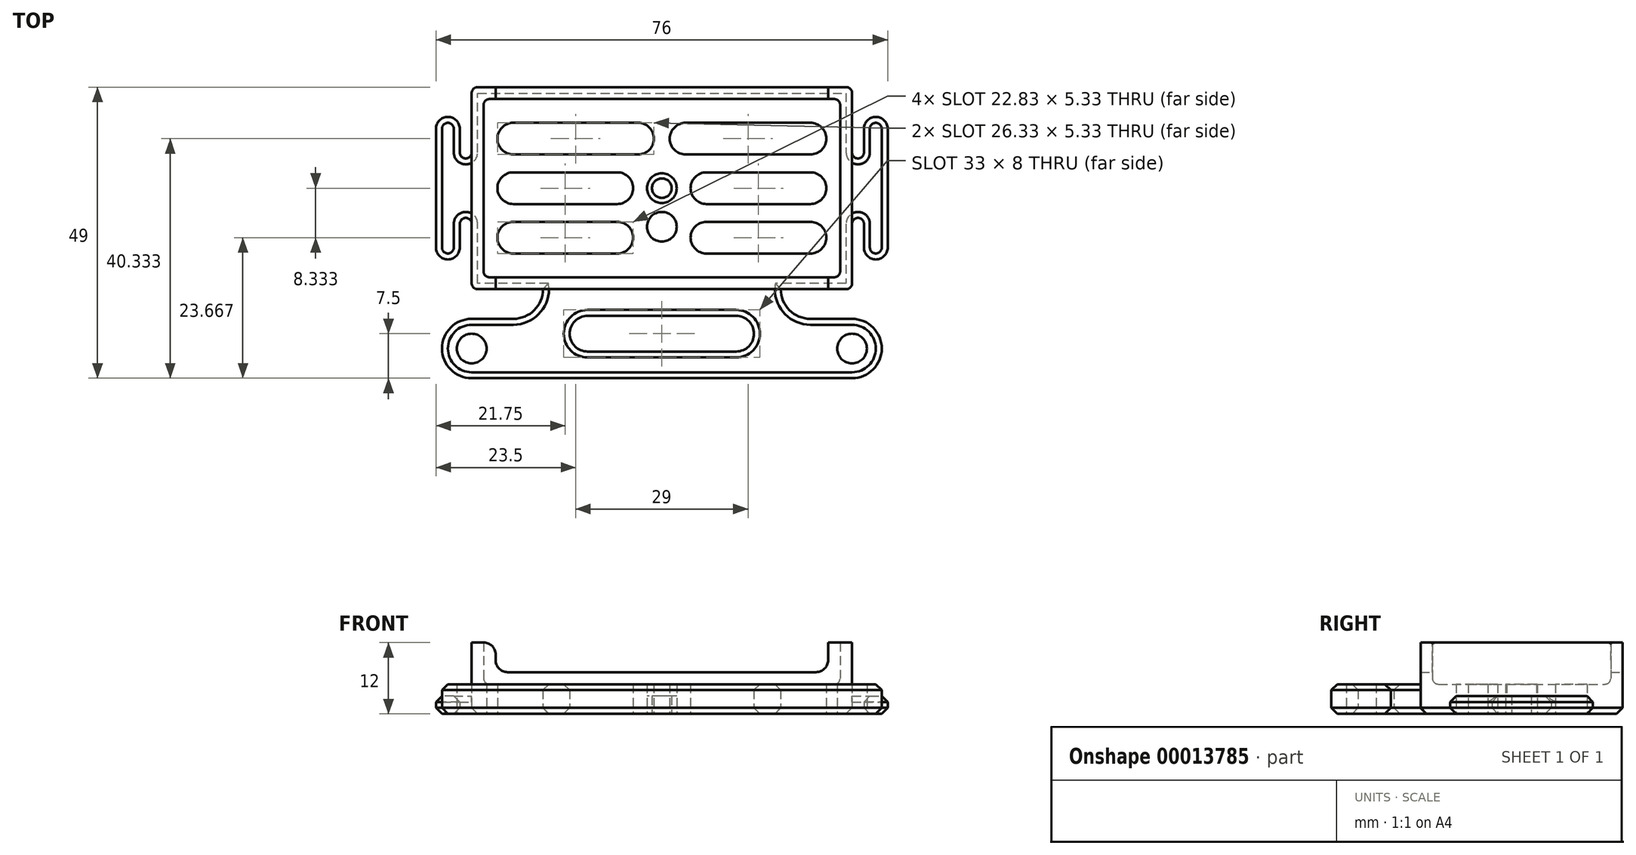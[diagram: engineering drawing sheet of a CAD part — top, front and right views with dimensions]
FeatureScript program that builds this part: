
annotation { "Feature Type Name" : "Feature", "Feature Type Description" : "" }
export const myFeature = defineFeature(function(context is Context, id is Id, definition is map)
    precondition{}
    {
        {
            var Q0;
            Q0=qCreatedBy(makeId("Top.planeOp"),FACE);
            var sketch = newSketch(context, id + "F0", { "sketchPlane" : qUnion([Q0])});
            skCircle(sketch, "E0", {"center": v(0, 0) * mm, "radius": 2.5 * mm});
            skCircle(sketch, "E1", {"center": v(0, -6.5) * mm, "radius": 2.5 * mm});
            skLineSegment(sketch, "E2", {"start": v(0, -6.5) * mm, "end": v(0, 17) * mm, "construction": true});
            skLineSegment(sketch, "E3.rect.bottom", {"start": v(-32, 17) * mm, "end": v(32, 17) * mm});
            skLineSegment(sketch, "E3.rect.top", {"start": v(-32, -17) * mm, "end": v(32, -17) * mm});
            skLineSegment(sketch, "E3.rect.left", {"start": v(-32, 17) * mm, "end": v(-32, -17) * mm});
            skLineSegment(sketch, "E3.rect.right", {"start": v(32, 17) * mm, "end": v(32, -17) * mm});
            skLineSegment(sketch, "E4.bottom", {"start": v(-32, -22) * mm, "end": v(-25, -22) * mm});
            skLineSegment(sketch, "E4.top", {"start": v(-32, -32) * mm, "end": v(32, -32) * mm});
            skLineSegment(sketch, "E4.left", {"start": v(-32, -22) * mm, "end": v(-32, -32) * mm, "construction": true});
            skLineSegment(sketch, "E4.right", {"start": v(32, -22) * mm, "end": v(32, -32) * mm, "construction": true});
            skCircle(sketch, "E5", {"center": v(-32, -27) * mm, "radius": 2.5 * mm});
            skArc(sketch, "E6", {"start": v(-32, -32) * mm, "mid": v(-37, -27) * mm, "end": v(-32, -22) * mm});
            skLineSegment(sketch, "E7", {"start": v(-20, -17) * mm, "end": v(-20, -17) * mm});
            skLineSegment(sketch, "E8.0.MirrorCS", {"start": v(20, -17) * mm, "end": v(20, -22) * mm});
            skCircle(sketch, "E9.0.MirrorC", {"center": v(32, -27) * mm, "radius": 2.5 * mm});
            skArc(sketch, "E10.0.MirrorCS", {"start": v(32, -32) * mm, "mid": v(37, -27) * mm, "end": v(32, -22) * mm});
            skPoint(sketch, "E11.newPointA", {"position": v(-20, -22) * mm});
            skArc(sketch, "E11.filletArc", {"start": v(-25, -22) * mm, "mid": v(-21.46, -20.54) * mm, "end": v(-20, -17) * mm});
            skArc(sketch, "E12.0.MirrorCS", {"start": v(25, -22) * mm, "mid": v(21.46, -20.54) * mm, "end": v(20, -17) * mm});
            skLineSegment(sketch, "E13", {"start": v(32, -22) * mm, "end": v(25, -22) * mm});
            skLineSegment(sketch, "E14.rect.bottom", {"start": v(12.5, -27.5) * mm, "end": v(-12.5, -27.5) * mm});
            skLineSegment(sketch, "E14.rect.top", {"start": v(12.5, -21.5) * mm, "end": v(-12.5, -21.5) * mm});
            skLineSegment(sketch, "E14.rect.left", {"start": v(12.5, -27.5) * mm, "end": v(12.5, -21.5) * mm, "construction": true});
            skLineSegment(sketch, "E14.rect.right", {"start": v(-12.5, -27.5) * mm, "end": v(-12.5, -21.5) * mm, "construction": true});
            skPoint(sketch, "E14.rect.middle", {"position": v(0, -24.5) * mm});
            skLineSegment(sketch, "E15", {"start": v(0, -17) * mm, "end": v(0, -32) * mm, "construction": true});
            skArc(sketch, "E16", {"start": v(-12.5, -21.5) * mm, "mid": v(-15.5, -24.5) * mm, "end": v(-12.5, -27.5) * mm});
            skArc(sketch, "E17", {"start": v(12.5, -21.5) * mm, "mid": v(15.5, -24.5) * mm, "end": v(12.5, -27.5) * mm});
            skLineSegment(sketch, "E18.0", {"start": v(-30, 15) * mm, "end": v(30, 15) * mm});
            skLineSegment(sketch, "E18.1", {"start": v(-30, 15) * mm, "end": v(-30, -15) * mm});
            skLineSegment(sketch, "E18.2", {"start": v(-30, -15) * mm, "end": v(30, -15) * mm});
            skLineSegment(sketch, "E18.3", {"start": v(30, 15) * mm, "end": v(30, -15) * mm});
            skLineSegment(sketch, "E19.rect.bottom", {"start": v(-38, 10) * mm, "end": v(-34, 10) * mm, "construction": true});
            skLineSegment(sketch, "E19.rect.top", {"start": v(-38, -10) * mm, "end": v(-34, -10) * mm, "construction": true});
            skLineSegment(sketch, "E19.rect.left", {"start": v(-38, 10) * mm, "end": v(-38, -10) * mm});
            skLineSegment(sketch, "E19.rect.right", {"start": v(-34, 10) * mm, "end": v(-34, 6) * mm});
            skPoint(sketch, "E19.rect.middle", {"position": v(-36, 0) * mm});
            skArc(sketch, "E20", {"start": v(-38, -10) * mm, "mid": v(-36, -12) * mm, "end": v(-34, -10) * mm});
            skArc(sketch, "E21", {"start": v(-38, 10) * mm, "mid": v(-36, 12) * mm, "end": v(-34, 10) * mm});
            skLineSegment(sketch, "E22", {"start": v(0, 0) * mm, "end": v(-36, 0) * mm, "construction": true});
            skArc(sketch, "E23.filletArc", {"start": v(-34, 6) * mm, "mid": v(-33, 5) * mm, "end": v(-32, 6) * mm});
            skArc(sketch, "E24.0.MirrorCS", {"start": v(-34, -6) * mm, "mid": v(-33, -5) * mm, "end": v(-32, -6) * mm});
            skLineSegment(sketch, "E25.0.MirrorCS", {"start": v(-34, -10) * mm, "end": v(-34, -6) * mm});
            skArc(sketch, "E26.0.MirrorCS", {"start": v(34, -6) * mm, "mid": v(33, -5) * mm, "end": v(32, -6) * mm});
            skLineSegment(sketch, "E26.1.MirrorCS", {"start": v(38, 10) * mm, "end": v(34, 10) * mm, "construction": true});
            skLineSegment(sketch, "E26.2.MirrorCS", {"start": v(38, -10) * mm, "end": v(34, -10) * mm, "construction": true});
            skArc(sketch, "E26.3.MirrorCS", {"start": v(38, 10) * mm, "mid": v(36, 12) * mm, "end": v(34, 10) * mm});
            skLineSegment(sketch, "E26.4.MirrorCS", {"start": v(34, -10) * mm, "end": v(34, -6) * mm});
            skLineSegment(sketch, "E26.5.MirrorCS", {"start": v(38, 10) * mm, "end": v(38, -10) * mm});
            skLineSegment(sketch, "E26.6.MirrorCS", {"start": v(34, 10) * mm, "end": v(34, 6) * mm});
            skArc(sketch, "E26.7.MirrorCS", {"start": v(38, -10) * mm, "mid": v(36, -12) * mm, "end": v(34, -10) * mm});
            skPoint(sketch, "E26.8.MirrorP", {"position": v(36, 0) * mm});
            skArc(sketch, "E26.9.MirrorCS", {"start": v(34, 6) * mm, "mid": v(33, 5) * mm, "end": v(32, 6) * mm});
            skLineSegment(sketch, "E27.bottom", {"start": v(-25, 11) * mm, "end": v(-4, 11) * mm});
            skLineSegment(sketch, "E27.top", {"start": v(-25, 5.67) * mm, "end": v(-4, 5.67) * mm});
            skLineSegment(sketch, "E27.left", {"start": v(-25, 11) * mm, "end": v(-25, 5.67) * mm, "construction": true});
            skLineSegment(sketch, "E27.right", {"start": v(-4, 11) * mm, "end": v(-4, 5.67) * mm, "construction": true});
            skLineSegment(sketch, "E28.bottom", {"start": v(-25, 2.67) * mm, "end": v(-7.5, 2.67) * mm});
            skLineSegment(sketch, "E28.top", {"start": v(-25, -2.67) * mm, "end": v(-7.5, -2.67) * mm});
            skLineSegment(sketch, "E28.left", {"start": v(-25, 2.67) * mm, "end": v(-25, -2.67) * mm, "construction": true});
            skLineSegment(sketch, "E28.right", {"start": v(-7.5, 2.67) * mm, "end": v(-7.5, -2.67) * mm, "construction": true});
            skLineSegment(sketch, "E29.bottom", {"start": v(-25, -5.67) * mm, "end": v(-7.5, -5.67) * mm});
            skLineSegment(sketch, "E29.top", {"start": v(-25, -11) * mm, "end": v(-7.5, -11) * mm});
            skLineSegment(sketch, "E29.left", {"start": v(-25, -5.67) * mm, "end": v(-25, -11) * mm, "construction": true});
            skLineSegment(sketch, "E29.right", {"start": v(-7.5, -5.67) * mm, "end": v(-7.5, -11) * mm, "construction": true});
            skPoint(sketch, "E30", {"position": v(-25, 0) * mm});
            skLineSegment(sketch, "E31.0.MirrorCS", {"start": v(25, -11) * mm, "end": v(7.5, -11) * mm});
            skLineSegment(sketch, "E32.0.MirrorCS", {"start": v(25, -5.67) * mm, "end": v(7.5, -5.67) * mm});
            skLineSegment(sketch, "E33.0.MirrorCS", {"start": v(25, -2.67) * mm, "end": v(7.5, -2.67) * mm});
            skLineSegment(sketch, "E34.0.MirrorCS", {"start": v(25, 2.67) * mm, "end": v(7.5, 2.67) * mm});
            skLineSegment(sketch, "E35.0.MirrorCS", {"start": v(25, 5.67) * mm, "end": v(4, 5.67) * mm});
            skLineSegment(sketch, "E36.0.MirrorCS", {"start": v(25, 11) * mm, "end": v(4, 11) * mm});
            skLineSegment(sketch, "E37.0.MirrorCS", {"start": v(4, 11) * mm, "end": v(4, 5.67) * mm, "construction": true});
            skLineSegment(sketch, "E38.0.MirrorCS", {"start": v(7.5, 2.67) * mm, "end": v(7.5, -2.67) * mm, "construction": true});
            skLineSegment(sketch, "E39.0.MirrorCS", {"start": v(7.5, -5.67) * mm, "end": v(7.5, -11) * mm, "construction": true});
            skLineSegment(sketch, "E40.0.MirrorCS", {"start": v(25, -5.67) * mm, "end": v(25, -11) * mm, "construction": true});
            skLineSegment(sketch, "E41.0.MirrorCS", {"start": v(25, 2.67) * mm, "end": v(25, -2.67) * mm, "construction": true});
            skLineSegment(sketch, "E42.0.MirrorCS", {"start": v(25, 11) * mm, "end": v(25, 5.67) * mm, "construction": true});
            skArc(sketch, "E43", {"start": v(-25, 11) * mm, "mid": v(-27.67, 8.33) * mm, "end": v(-25, 5.67) * mm});
            skArc(sketch, "E44", {"start": v(-25, 2.67) * mm, "mid": v(-27.67, 0) * mm, "end": v(-25, -2.67) * mm});
            skArc(sketch, "E45", {"start": v(-25, -5.67) * mm, "mid": v(-27.67, -8.33) * mm, "end": v(-25, -11) * mm});
            skArc(sketch, "E46", {"start": v(-4, 11) * mm, "mid": v(-1.33, 8.33) * mm, "end": v(-4, 5.67) * mm});
            skArc(sketch, "E47", {"start": v(-7.5, 2.67) * mm, "mid": v(-4.83, 0) * mm, "end": v(-7.5, -2.67) * mm});
            skArc(sketch, "E48", {"start": v(-7.5, -5.67) * mm, "mid": v(-4.83, -8.33) * mm, "end": v(-7.5, -11) * mm});
            skArc(sketch, "E49.0.MirrorCS", {"start": v(4, 11) * mm, "mid": v(1.33, 8.33) * mm, "end": v(4, 5.67) * mm});
            skArc(sketch, "E50.0.MirrorCS", {"start": v(7.5, 2.67) * mm, "mid": v(4.83, 0) * mm, "end": v(7.5, -2.67) * mm});
            skArc(sketch, "E51.0.MirrorCS", {"start": v(7.5, -5.67) * mm, "mid": v(4.83, -8.33) * mm, "end": v(7.5, -11) * mm});
            skArc(sketch, "E52.0.MirrorCS", {"start": v(25, 11) * mm, "mid": v(27.67, 8.33) * mm, "end": v(25, 5.67) * mm});
            skArc(sketch, "E53.0.MirrorCS", {"start": v(25, 2.67) * mm, "mid": v(27.67, 0) * mm, "end": v(25, -2.67) * mm});
            skArc(sketch, "E54.0.MirrorCS", {"start": v(25, -5.67) * mm, "mid": v(27.67, -8.33) * mm, "end": v(25, -11) * mm});
            skCircle(sketch, "E55", {"center": v(0, 0) * mm, "radius": 1.65 * mm});
            skSolve(sketch);
        }
        {
            var Q0;
            Q0=makeQuery(id+"F0.imprint","IMPRINT",FACE,{"disambiguationData":[TD([[makeQuery(id+"F0.imprint","IMPRINT",EDGE,{"derivedFrom":sQuery(id+"F0.wireOp",EDGE,"E4.bottom")}),-1.0]])]});
            var Q1;
            Q1=makeQuery(id+"F0.imprint","IMPRINT",FACE,{"disambiguationData":[TD([[makeQuery(id+"F0.imprint","IMPRINT",EDGE,{"derivedFrom":sQuery(id+"F0.wireOp",EDGE,"E0")}),-1.0]])]});
            var Q2;
            {var subQ5=sQuery(id+"F0.wireOp",EDGE,"E3.rect.bottom");Q2=makeQuery(id+"F0.imprint","IMPRINT",FACE,{"disambiguationData":[TD([[makeQuery(id+"F0.imprint","IMPRINT",EDGE,{"derivedFrom":subQ5}),-1.0]])]});}
            extrude(context, id + "F1", {"entities" : qUnion([Q0, Q1, Q2]), "depth" : 5 * mm});
        }
        {
            var Q0;
            Q0=makeQuery(id+"F0.imprint","IMPRINT",FACE,{"disambiguationData":[TD([[makeQuery(id+"F0.imprint","IMPRINT",EDGE,{"derivedFrom":sQuery(id+"F0.wireOp",EDGE,"E19.rect.left")}),1.0]])]});
            var Q1;
            {var subQ1=sQuery(id+"F0.wireOp",EDGE,"E26.0.MirrorCS");Q1=makeQuery(id+"F0.imprint","IMPRINT",FACE,{"disambiguationData":[TD([[makeQuery(id+"F0.imprint","IMPRINT",EDGE,{"derivedFrom":subQ1}),-1.0]])]});}
            var Q2;
            Q2=makeQuery(id+"F0.imprint","IMPRINT",FACE,{"disambiguationData":[TD([[makeQuery(id+"F0.imprint","IMPRINT",EDGE,{"derivedFrom":sQuery(id+"F0.wireOp",EDGE,"E0")}),1.0]])]});
            extrude(context, id + "F2", {"entities" : qUnion([Q0, Q1, Q2]), "operationType" : NewBodyOperationType.ADD, "depth" : 3 * mm});
        }
        {
            var Q0;
            {var subQ5=sQuery(id+"F0.wireOp",EDGE,"E3.rect.bottom");Q0=makeQuery(id+"F0.imprint","IMPRINT",FACE,{"disambiguationData":[TD([[makeQuery(id+"F0.imprint","IMPRINT",EDGE,{"derivedFrom":subQ5}),-1.0]])]});}
            extrude(context, id + "F3", {"entities" : qUnion([Q0]), "operationType" : NewBodyOperationType.ADD, "depth" : 12 * mm});
        }
        {
            var Q0;
            Q0=makeQuery(id+"F3.opExtrude","SWEPT_FACE",FACE,{"disambiguationData":[OSD([sQuery(id+"F0.wireOp",EDGE,"E18.2")])]});
            var sketch = newSketch(context, id + "F4", { "sketchPlane" : qUnion([Q0])});
            skLineSegment(sketch, "E56.bottom", {"start": v(-30, 5) * mm, "end": v(30, 5) * mm, "construction": true});
            skLineSegment(sketch, "E56.top", {"start": v(-30, 12) * mm, "end": v(30, 12) * mm});
            skLineSegment(sketch, "E56.left", {"start": v(-30, 5) * mm, "end": v(-30, 12) * mm, "construction": true});
            skLineSegment(sketch, "E56.right", {"start": v(30, 5) * mm, "end": v(30, 12) * mm, "construction": true});
            skLineSegment(sketch, "E57.0", {"start": v(-27.97, 7.03) * mm, "end": v(27.97, 7.03) * mm});
            skLineSegment(sketch, "E57.1", {"start": v(-27.97, 7.03) * mm, "end": v(-27.97, 12) * mm});
            skLineSegment(sketch, "E58", {"start": v(0, 0) * mm, "end": v(0, 12) * mm, "construction": true});
            skLineSegment(sketch, "E59.0.MirrorCS", {"start": v(27.97, 7.03) * mm, "end": v(27.97, 12) * mm});
            skSolve(sketch);
        }
        {
            var Q0;
            Q0=makeQuery(id+"F4.imprint","IMPRINT",FACE,{"disambiguationData":[TD([[makeQuery(id+"F4.imprint","IMPRINT",EDGE,{"derivedFrom":sQuery(id+"F4.wireOp",EDGE,"E57.0")}),1.0]])]});
            var Q1;
            Q1=sQuery(id+"F4.wireOp",EDGE,"E56.top");
            extrude(context, id + "F5", {"entities" : qUnion([Q0]), "operationType" : NewBodyOperationType.REMOVE, "surfaceEntities" : qUnion([Q1]), "endBound" : BoundingType.SYMMETRIC, "oppositeDirection" : true, "depth" : 99.9 * mm});
        }
        {
            var Q0;
            Q0=makeQuery(id+"F3.boolean.opBoolean","INTERSECT",EDGE,{"derivedFrom":[makeQuery(id+"F1.opExtrude","CAP_FACE",FACE,{"disambiguationData":[OSD([sQuery(id+"F0.wireOp",EDGE,"E0"),sQuery(id+"F0.wireOp",EDGE,"E1"),sQuery(id+"F0.wireOp",EDGE,"E3.rect.bottom"),sQuery(id+"F0.wireOp",EDGE,"E3.rect.top"),sQuery(id+"F0.wireOp",EDGE,"E3.rect.left"),sQuery(id+"F0.wireOp",EDGE,"E3.rect.right"),sQuery(id+"F0.wireOp",EDGE,"E4.bottom"),sQuery(id+"F0.wireOp",EDGE,"E4.top"),sQuery(id+"F0.wireOp",EDGE,"E5"),sQuery(id+"F0.wireOp",EDGE,"E6"),sQuery(id+"F0.wireOp",EDGE,"E9.0.MirrorC"),sQuery(id+"F0.wireOp",EDGE,"E10.0.MirrorCS"),sQuery(id+"F0.wireOp",EDGE,"E11.filletArc"),sQuery(id+"F0.wireOp",EDGE,"E12.0.MirrorCS"),sQuery(id+"F0.wireOp",EDGE,"E13"),sQuery(id+"F0.wireOp",EDGE,"E14.rect.bottom"),sQuery(id+"F0.wireOp",EDGE,"E14.rect.top"),sQuery(id+"F0.wireOp",EDGE,"E16"),sQuery(id+"F0.wireOp",EDGE,"E17"),sQuery(id+"F0.wireOp",EDGE,"E27.bottom"),sQuery(id+"F0.wireOp",EDGE,"E27.top"),sQuery(id+"F0.wireOp",EDGE,"E28.bottom"),sQuery(id+"F0.wireOp",EDGE,"E28.top"),sQuery(id+"F0.wireOp",EDGE,"E29.bottom"),sQuery(id+"F0.wireOp",EDGE,"E29.top"),sQuery(id+"F0.wireOp",EDGE,"E31.0.MirrorCS"),sQuery(id+"F0.wireOp",EDGE,"E32.0.MirrorCS"),sQuery(id+"F0.wireOp",EDGE,"E33.0.MirrorCS"),sQuery(id+"F0.wireOp",EDGE,"E34.0.MirrorCS"),sQuery(id+"F0.wireOp",EDGE,"E35.0.MirrorCS"),sQuery(id+"F0.wireOp",EDGE,"E36.0.MirrorCS"),sQuery(id+"F0.wireOp",EDGE,"E43"),sQuery(id+"F0.wireOp",EDGE,"E44"),sQuery(id+"F0.wireOp",EDGE,"E45"),sQuery(id+"F0.wireOp",EDGE,"E46"),sQuery(id+"F0.wireOp",EDGE,"E47"),sQuery(id+"F0.wireOp",EDGE,"E48"),sQuery(id+"F0.wireOp",EDGE,"E49.0.MirrorCS"),sQuery(id+"F0.wireOp",EDGE,"E50.0.MirrorCS"),sQuery(id+"F0.wireOp",EDGE,"E51.0.MirrorCS"),sQuery(id+"F0.wireOp",EDGE,"E52.0.MirrorCS"),sQuery(id+"F0.wireOp",EDGE,"E53.0.MirrorCS"),sQuery(id+"F0.wireOp",EDGE,"E54.0.MirrorCS")])],"isStart":false}),makeQuery(id+"F3.opExtrude","SWEPT_FACE",FACE,{"disambiguationData":[OSD([sQuery(id+"F0.wireOp",EDGE,"E18.1")])]})]});
            var Q1;
            Q1=makeQuery(id+"F3.boolean.opBoolean","INTERSECT",EDGE,{"derivedFrom":[makeQuery(id+"F1.opExtrude","CAP_FACE",FACE,{"disambiguationData":[OSD([sQuery(id+"F0.wireOp",EDGE,"E0"),sQuery(id+"F0.wireOp",EDGE,"E1"),sQuery(id+"F0.wireOp",EDGE,"E3.rect.bottom"),sQuery(id+"F0.wireOp",EDGE,"E3.rect.top"),sQuery(id+"F0.wireOp",EDGE,"E3.rect.left"),sQuery(id+"F0.wireOp",EDGE,"E3.rect.right"),sQuery(id+"F0.wireOp",EDGE,"E4.bottom"),sQuery(id+"F0.wireOp",EDGE,"E4.top"),sQuery(id+"F0.wireOp",EDGE,"E5"),sQuery(id+"F0.wireOp",EDGE,"E6"),sQuery(id+"F0.wireOp",EDGE,"E9.0.MirrorC"),sQuery(id+"F0.wireOp",EDGE,"E10.0.MirrorCS"),sQuery(id+"F0.wireOp",EDGE,"E11.filletArc"),sQuery(id+"F0.wireOp",EDGE,"E12.0.MirrorCS"),sQuery(id+"F0.wireOp",EDGE,"E13"),sQuery(id+"F0.wireOp",EDGE,"E14.rect.bottom"),sQuery(id+"F0.wireOp",EDGE,"E14.rect.top"),sQuery(id+"F0.wireOp",EDGE,"E16"),sQuery(id+"F0.wireOp",EDGE,"E17"),sQuery(id+"F0.wireOp",EDGE,"E27.bottom"),sQuery(id+"F0.wireOp",EDGE,"E27.top"),sQuery(id+"F0.wireOp",EDGE,"E28.bottom"),sQuery(id+"F0.wireOp",EDGE,"E28.top"),sQuery(id+"F0.wireOp",EDGE,"E29.bottom"),sQuery(id+"F0.wireOp",EDGE,"E29.top"),sQuery(id+"F0.wireOp",EDGE,"E31.0.MirrorCS"),sQuery(id+"F0.wireOp",EDGE,"E32.0.MirrorCS"),sQuery(id+"F0.wireOp",EDGE,"E33.0.MirrorCS"),sQuery(id+"F0.wireOp",EDGE,"E34.0.MirrorCS"),sQuery(id+"F0.wireOp",EDGE,"E35.0.MirrorCS"),sQuery(id+"F0.wireOp",EDGE,"E36.0.MirrorCS"),sQuery(id+"F0.wireOp",EDGE,"E43"),sQuery(id+"F0.wireOp",EDGE,"E44"),sQuery(id+"F0.wireOp",EDGE,"E45"),sQuery(id+"F0.wireOp",EDGE,"E46"),sQuery(id+"F0.wireOp",EDGE,"E47"),sQuery(id+"F0.wireOp",EDGE,"E48"),sQuery(id+"F0.wireOp",EDGE,"E49.0.MirrorCS"),sQuery(id+"F0.wireOp",EDGE,"E50.0.MirrorCS"),sQuery(id+"F0.wireOp",EDGE,"E51.0.MirrorCS"),sQuery(id+"F0.wireOp",EDGE,"E52.0.MirrorCS"),sQuery(id+"F0.wireOp",EDGE,"E53.0.MirrorCS"),sQuery(id+"F0.wireOp",EDGE,"E54.0.MirrorCS")])],"isStart":false}),makeQuery(id+"F3.opExtrude","SWEPT_FACE",FACE,{"disambiguationData":[OSD([sQuery(id+"F0.wireOp",EDGE,"E18.0")])]})]});
            var Q2;
            Q2=makeQuery(id+"F3.boolean.opBoolean","INTERSECT",EDGE,{"derivedFrom":[makeQuery(id+"F1.opExtrude","CAP_FACE",FACE,{"disambiguationData":[OSD([sQuery(id+"F0.wireOp",EDGE,"E0"),sQuery(id+"F0.wireOp",EDGE,"E1"),sQuery(id+"F0.wireOp",EDGE,"E3.rect.bottom"),sQuery(id+"F0.wireOp",EDGE,"E3.rect.top"),sQuery(id+"F0.wireOp",EDGE,"E3.rect.left"),sQuery(id+"F0.wireOp",EDGE,"E3.rect.right"),sQuery(id+"F0.wireOp",EDGE,"E4.bottom"),sQuery(id+"F0.wireOp",EDGE,"E4.top"),sQuery(id+"F0.wireOp",EDGE,"E5"),sQuery(id+"F0.wireOp",EDGE,"E6"),sQuery(id+"F0.wireOp",EDGE,"E9.0.MirrorC"),sQuery(id+"F0.wireOp",EDGE,"E10.0.MirrorCS"),sQuery(id+"F0.wireOp",EDGE,"E11.filletArc"),sQuery(id+"F0.wireOp",EDGE,"E12.0.MirrorCS"),sQuery(id+"F0.wireOp",EDGE,"E13"),sQuery(id+"F0.wireOp",EDGE,"E14.rect.bottom"),sQuery(id+"F0.wireOp",EDGE,"E14.rect.top"),sQuery(id+"F0.wireOp",EDGE,"E16"),sQuery(id+"F0.wireOp",EDGE,"E17"),sQuery(id+"F0.wireOp",EDGE,"E27.bottom"),sQuery(id+"F0.wireOp",EDGE,"E27.top"),sQuery(id+"F0.wireOp",EDGE,"E28.bottom"),sQuery(id+"F0.wireOp",EDGE,"E28.top"),sQuery(id+"F0.wireOp",EDGE,"E29.bottom"),sQuery(id+"F0.wireOp",EDGE,"E29.top"),sQuery(id+"F0.wireOp",EDGE,"E31.0.MirrorCS"),sQuery(id+"F0.wireOp",EDGE,"E32.0.MirrorCS"),sQuery(id+"F0.wireOp",EDGE,"E33.0.MirrorCS"),sQuery(id+"F0.wireOp",EDGE,"E34.0.MirrorCS"),sQuery(id+"F0.wireOp",EDGE,"E35.0.MirrorCS"),sQuery(id+"F0.wireOp",EDGE,"E36.0.MirrorCS"),sQuery(id+"F0.wireOp",EDGE,"E43"),sQuery(id+"F0.wireOp",EDGE,"E44"),sQuery(id+"F0.wireOp",EDGE,"E45"),sQuery(id+"F0.wireOp",EDGE,"E46"),sQuery(id+"F0.wireOp",EDGE,"E47"),sQuery(id+"F0.wireOp",EDGE,"E48"),sQuery(id+"F0.wireOp",EDGE,"E49.0.MirrorCS"),sQuery(id+"F0.wireOp",EDGE,"E50.0.MirrorCS"),sQuery(id+"F0.wireOp",EDGE,"E51.0.MirrorCS"),sQuery(id+"F0.wireOp",EDGE,"E52.0.MirrorCS"),sQuery(id+"F0.wireOp",EDGE,"E53.0.MirrorCS"),sQuery(id+"F0.wireOp",EDGE,"E54.0.MirrorCS")])],"isStart":false}),makeQuery(id+"F3.opExtrude","SWEPT_FACE",FACE,{"disambiguationData":[OSD([sQuery(id+"F0.wireOp",EDGE,"E18.2")])]})]});
            var Q3;
            Q3=makeQuery(id+"F3.boolean.opBoolean","INTERSECT",EDGE,{"derivedFrom":[makeQuery(id+"F1.opExtrude","CAP_FACE",FACE,{"disambiguationData":[OSD([sQuery(id+"F0.wireOp",EDGE,"E0"),sQuery(id+"F0.wireOp",EDGE,"E1"),sQuery(id+"F0.wireOp",EDGE,"E3.rect.bottom"),sQuery(id+"F0.wireOp",EDGE,"E3.rect.top"),sQuery(id+"F0.wireOp",EDGE,"E3.rect.left"),sQuery(id+"F0.wireOp",EDGE,"E3.rect.right"),sQuery(id+"F0.wireOp",EDGE,"E4.bottom"),sQuery(id+"F0.wireOp",EDGE,"E4.top"),sQuery(id+"F0.wireOp",EDGE,"E5"),sQuery(id+"F0.wireOp",EDGE,"E6"),sQuery(id+"F0.wireOp",EDGE,"E9.0.MirrorC"),sQuery(id+"F0.wireOp",EDGE,"E10.0.MirrorCS"),sQuery(id+"F0.wireOp",EDGE,"E11.filletArc"),sQuery(id+"F0.wireOp",EDGE,"E12.0.MirrorCS"),sQuery(id+"F0.wireOp",EDGE,"E13"),sQuery(id+"F0.wireOp",EDGE,"E14.rect.bottom"),sQuery(id+"F0.wireOp",EDGE,"E14.rect.top"),sQuery(id+"F0.wireOp",EDGE,"E16"),sQuery(id+"F0.wireOp",EDGE,"E17"),sQuery(id+"F0.wireOp",EDGE,"E27.bottom"),sQuery(id+"F0.wireOp",EDGE,"E27.top"),sQuery(id+"F0.wireOp",EDGE,"E28.bottom"),sQuery(id+"F0.wireOp",EDGE,"E28.top"),sQuery(id+"F0.wireOp",EDGE,"E29.bottom"),sQuery(id+"F0.wireOp",EDGE,"E29.top"),sQuery(id+"F0.wireOp",EDGE,"E31.0.MirrorCS"),sQuery(id+"F0.wireOp",EDGE,"E32.0.MirrorCS"),sQuery(id+"F0.wireOp",EDGE,"E33.0.MirrorCS"),sQuery(id+"F0.wireOp",EDGE,"E34.0.MirrorCS"),sQuery(id+"F0.wireOp",EDGE,"E35.0.MirrorCS"),sQuery(id+"F0.wireOp",EDGE,"E36.0.MirrorCS"),sQuery(id+"F0.wireOp",EDGE,"E43"),sQuery(id+"F0.wireOp",EDGE,"E44"),sQuery(id+"F0.wireOp",EDGE,"E45"),sQuery(id+"F0.wireOp",EDGE,"E46"),sQuery(id+"F0.wireOp",EDGE,"E47"),sQuery(id+"F0.wireOp",EDGE,"E48"),sQuery(id+"F0.wireOp",EDGE,"E49.0.MirrorCS"),sQuery(id+"F0.wireOp",EDGE,"E50.0.MirrorCS"),sQuery(id+"F0.wireOp",EDGE,"E51.0.MirrorCS"),sQuery(id+"F0.wireOp",EDGE,"E52.0.MirrorCS"),sQuery(id+"F0.wireOp",EDGE,"E53.0.MirrorCS"),sQuery(id+"F0.wireOp",EDGE,"E54.0.MirrorCS")])],"isStart":false}),makeQuery(id+"F3.opExtrude","SWEPT_FACE",FACE,{"disambiguationData":[OSD([sQuery(id+"F0.wireOp",EDGE,"E18.3")])]})]});
            var Q4;
            Q4=makeQuery(id+"F3.opExtrude","SWEPT_EDGE",EDGE,{"disambiguationData":[OSD([sQuery(id+"F0.wireOp",EDGE,"E18.0"),sQuery(id+"F0.wireOp",EDGE,"E18.3")])]});
            var Q5;
            Q5=makeQuery(id+"F3.opExtrude","SWEPT_EDGE",EDGE,{"disambiguationData":[OSD([sQuery(id+"F0.wireOp",EDGE,"E18.0"),sQuery(id+"F0.wireOp",EDGE,"E18.1")])]});
            var Q6;
            Q6=makeQuery(id+"F3.opExtrude","SWEPT_EDGE",EDGE,{"disambiguationData":[OSD([sQuery(id+"F0.wireOp",EDGE,"E18.1"),sQuery(id+"F0.wireOp",EDGE,"E18.2")])]});
            var Q7;
            Q7=makeQuery(id+"F3.opExtrude","SWEPT_EDGE",EDGE,{"disambiguationData":[OSD([sQuery(id+"F0.wireOp",EDGE,"E18.2"),sQuery(id+"F0.wireOp",EDGE,"E18.3")])]});
            var Q8;
            {var subQ0=sQuery(id+"F0.wireOp",EDGE,"E3.rect.bottom");var subQ1=sQuery(id+"F0.wireOp",EDGE,"E3.rect.right");Q8=makeQuery(id+"F3.boolean.opBoolean","MERGE",EDGE,{"derivedFrom":[makeQuery(id+"F1.opExtrude","SWEPT_EDGE",EDGE,{"disambiguationData":[OSD([subQ0,subQ1])]}),makeQuery(id+"F3.opExtrude","SWEPT_EDGE",EDGE,{"disambiguationData":[OSD([subQ0,subQ1])]})]});}
            var Q9;
            {var subQ0=sQuery(id+"F0.wireOp",EDGE,"E3.rect.bottom");var subQ1=sQuery(id+"F0.wireOp",EDGE,"E3.rect.left");Q9=makeQuery(id+"F3.boolean.opBoolean","MERGE",EDGE,{"derivedFrom":[makeQuery(id+"F1.opExtrude","SWEPT_EDGE",EDGE,{"disambiguationData":[OSD([subQ0,subQ1])]}),makeQuery(id+"F3.opExtrude","SWEPT_EDGE",EDGE,{"disambiguationData":[OSD([subQ0,subQ1])]})]});}
            var Q10;
            {var subQ0=sQuery(id+"F0.wireOp",EDGE,"E3.rect.top");var subQ1=sQuery(id+"F0.wireOp",EDGE,"E3.rect.left");Q10=makeQuery(id+"F3.boolean.opBoolean","MERGE",EDGE,{"derivedFrom":[makeQuery(id+"F1.opExtrude","SWEPT_EDGE",EDGE,{"disambiguationData":[OSD([subQ0,subQ1])]}),makeQuery(id+"F3.opExtrude","SWEPT_EDGE",EDGE,{"disambiguationData":[OSD([subQ0,subQ1])]})]});}
            var Q11;
            {var subQ0=sQuery(id+"F0.wireOp",EDGE,"E3.rect.top");var subQ1=sQuery(id+"F0.wireOp",EDGE,"E3.rect.right");Q11=makeQuery(id+"F3.boolean.opBoolean","MERGE",EDGE,{"derivedFrom":[makeQuery(id+"F1.opExtrude","SWEPT_EDGE",EDGE,{"disambiguationData":[OSD([subQ0,subQ1])]}),makeQuery(id+"F3.opExtrude","SWEPT_EDGE",EDGE,{"disambiguationData":[OSD([subQ0,subQ1])]})]});}
            fillet(context, id + "F6", {"entities" : qUnion([Q0, Q1, Q2, Q3, Q4, Q5, Q6, Q7, Q8, Q9, Q10, Q11]), "radius" : 1 * mm, "tangentPropagation" : true, "allowEdgeOverflow" : false});
        }
        {
            var Q0;
            Q0=makeQuery(id+"F5.boolean.opBoolean","COPY",EDGE,{"disambiguationData":[OD(0.0)],"derivedFrom":makeQuery(id+"F5.opExtrude","SWEPT_EDGE",EDGE,{"disambiguationData":[OSD([sQuery(id+"F4.wireOp",EDGE,"E56.top"),sQuery(id+"F4.wireOp",EDGE,"E57.1")])]})});
            var Q1;
            Q1=makeQuery(id+"F5.boolean.opBoolean","COPY",EDGE,{"disambiguationData":[OD(0.0)],"derivedFrom":makeQuery(id+"F5.opExtrude","SWEPT_EDGE",EDGE,{"disambiguationData":[OSD([sQuery(id+"F4.wireOp",EDGE,"E57.0"),sQuery(id+"F4.wireOp",EDGE,"E57.1")])]})});
            var Q2;
            Q2=makeQuery(id+"F5.boolean.opBoolean","COPY",EDGE,{"disambiguationData":[OD(1.0)],"derivedFrom":makeQuery(id+"F5.opExtrude","SWEPT_EDGE",EDGE,{"disambiguationData":[OSD([sQuery(id+"F4.wireOp",EDGE,"E56.top"),sQuery(id+"F4.wireOp",EDGE,"E57.1")])]})});
            var Q3;
            Q3=makeQuery(id+"F5.boolean.opBoolean","COPY",EDGE,{"disambiguationData":[OD(1.0)],"derivedFrom":makeQuery(id+"F5.opExtrude","SWEPT_EDGE",EDGE,{"disambiguationData":[OSD([sQuery(id+"F4.wireOp",EDGE,"E57.0"),sQuery(id+"F4.wireOp",EDGE,"E57.1")])]})});
            var Q4;
            Q4=makeQuery(id+"F5.boolean.opBoolean","COPY",EDGE,{"disambiguationData":[OD(1.0)],"derivedFrom":makeQuery(id+"F5.opExtrude","SWEPT_EDGE",EDGE,{"disambiguationData":[OSD([sQuery(id+"F4.wireOp",EDGE,"E57.0"),sQuery(id+"F4.wireOp",EDGE,"E59.0.MirrorCS")])]})});
            var Q5;
            Q5=makeQuery(id+"F5.boolean.opBoolean","COPY",EDGE,{"disambiguationData":[OD(1.0)],"derivedFrom":makeQuery(id+"F5.opExtrude","SWEPT_EDGE",EDGE,{"disambiguationData":[OSD([sQuery(id+"F4.wireOp",EDGE,"E56.top"),sQuery(id+"F4.wireOp",EDGE,"E59.0.MirrorCS")])]})});
            var Q6;
            Q6=makeQuery(id+"F5.boolean.opBoolean","COPY",EDGE,{"disambiguationData":[OD(0.0)],"derivedFrom":makeQuery(id+"F5.opExtrude","SWEPT_EDGE",EDGE,{"disambiguationData":[OSD([sQuery(id+"F4.wireOp",EDGE,"E57.0"),sQuery(id+"F4.wireOp",EDGE,"E59.0.MirrorCS")])]})});
            var Q7;
            Q7=makeQuery(id+"F5.boolean.opBoolean","COPY",EDGE,{"disambiguationData":[OD(0.0)],"derivedFrom":makeQuery(id+"F5.opExtrude","SWEPT_EDGE",EDGE,{"disambiguationData":[OSD([sQuery(id+"F4.wireOp",EDGE,"E56.top"),sQuery(id+"F4.wireOp",EDGE,"E59.0.MirrorCS")])]})});
            fillet(context, id + "F7", {"entities" : qUnion([Q0, Q1, Q2, Q3, Q4, Q5, Q6, Q7]), "radius" : 2 * mm, "tangentPropagation" : true, "allowEdgeOverflow" : false});
        }
        {
            var Q0;
            Q0=makeQuery(id+"F1.opExtrude","CAP_EDGE",EDGE,{"disambiguationData":[OSD([sQuery(id+"F0.wireOp",EDGE,"E3.rect.bottom")])],"isStart":true});
            var Q1;
            Q1=makeQuery(id+"F1.opExtrude","CAP_EDGE",EDGE,{"disambiguationData":[OSD([sQuery(id+"F0.wireOp",EDGE,"E4.top")])],"isStart":true});
            var Q2;
            Q2=makeQuery(id+"F1.opExtrude","CAP_EDGE",EDGE,{"disambiguationData":[OSD([sQuery(id+"F0.wireOp",EDGE,"E4.top")])],"isStart":false});
            var Q3;
            Q3=makeQuery(id+"F1.opExtrude","CAP_EDGE",EDGE,{"disambiguationData":[OSD([sQuery(id+"F0.wireOp",EDGE,"E14.rect.bottom")])],"isStart":false});
            var Q4;
            Q4=makeQuery(id+"F1.opExtrude","CAP_EDGE",EDGE,{"disambiguationData":[OSD([sQuery(id+"F0.wireOp",EDGE,"E14.rect.bottom")])],"isStart":true});
            var Q5;
            Q5=makeQuery(id+"F2.opExtrude","CAP_EDGE",EDGE,{"disambiguationData":[OSD([sQuery(id+"F0.wireOp",EDGE,"E19.rect.left")])],"isStart":false});
            var Q6;
            Q6=makeQuery(id+"F2.opExtrude","CAP_EDGE",EDGE,{"disambiguationData":[OSD([sQuery(id+"F0.wireOp",EDGE,"E26.5.MirrorCS")])],"isStart":false});
            chamfer(context, id + "F8", {"entities" : qUnion([Q0, Q1, Q2, Q3, Q4, Q5, Q6]), "width" : 1 * mm, "tangentPropagation" : true});
        }
    });
